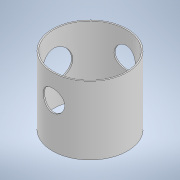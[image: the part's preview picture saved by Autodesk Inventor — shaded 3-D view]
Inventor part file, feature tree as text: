
AUTODESK INVENTOR PART (.ipt)
format: ipt  version: 2021 (Build 250183000, 183)  size: 135,680 bytes
history: native  units: mm
features: extrude x3, sketch x3
ambient origin geometry x8: Origin, YZ Plane, XZ Plane, XY Plane, X Axis, Y Axis, Z Axis, Center Point
bodies: Solid1 (feature_tree)
feature tree (6):
  extrude  "Extrusion1"  Depth=149.0mm
  extrude  "Extrusion2"  Depth=64.0mm
  extrude  "Extrusion3"  TaperAngle=0.0deg  [1 undecoded]
  sketch  "Sketch1"  dims[d0=154.0mm d1=149.0mm]
  sketch  "Sketch2"  dims[d2=140.0mm d3=0.0mm d4=64.0mm]
  sketch  "Sketch3"  dims[d5=75.0mm d6=0.0mm d7=0.0mm d8=44.0mm d9=90.0mm d10=0.0mm d11=0.0mm]
note: 1 required parameter value undecoded (feature->parameter linkage not recoverable at this tier; creation-order binding heuristic only, values carry confidence <= 0.55)
